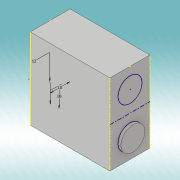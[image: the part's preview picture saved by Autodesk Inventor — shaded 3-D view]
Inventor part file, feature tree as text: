
AUTODESK INVENTOR PART (.ipt)
format: ipt  version: 2019 (Build 230136000, 136)  size: 118,272 bytes
history: native  units: mm
features: extrude x5, sketch x3
ambient origin geometry x8: Origin, YZ Plane, XZ Plane, XY Plane, X Axis, Y Axis, Z Axis, Center Point
bodies: Solid1 (feature_tree)
feature tree (8):
  extrude  "Extrusion1"  Depth=40.5mm
  sketch  "Sketch2"  dims[d2=20.0mm d3=0.0mm d4=12.0mm]
  extrude  "Extrusion2"  Depth=20.0mm
  sketch  "Sketch3"  dims[d5=10.0mm d6=10.0mm d7=1.5mm d8=0.0mm d11=1.5mm d12=0.0mm d13=0.1mm d14=0.0mm d15=0.1mm d16=0.0mm]
  extrude  "Extrusion4"  Depth=10.0mm
  extrude  "Extrusion5"  Depth=1.5mm TaperAngle=0.0deg
  extrude  "Extrusion6"  Depth=1.5mm TaperAngle=0.0deg
  sketch  "Sketch1"  dims[d0=40.0mm d1=40.5mm]
